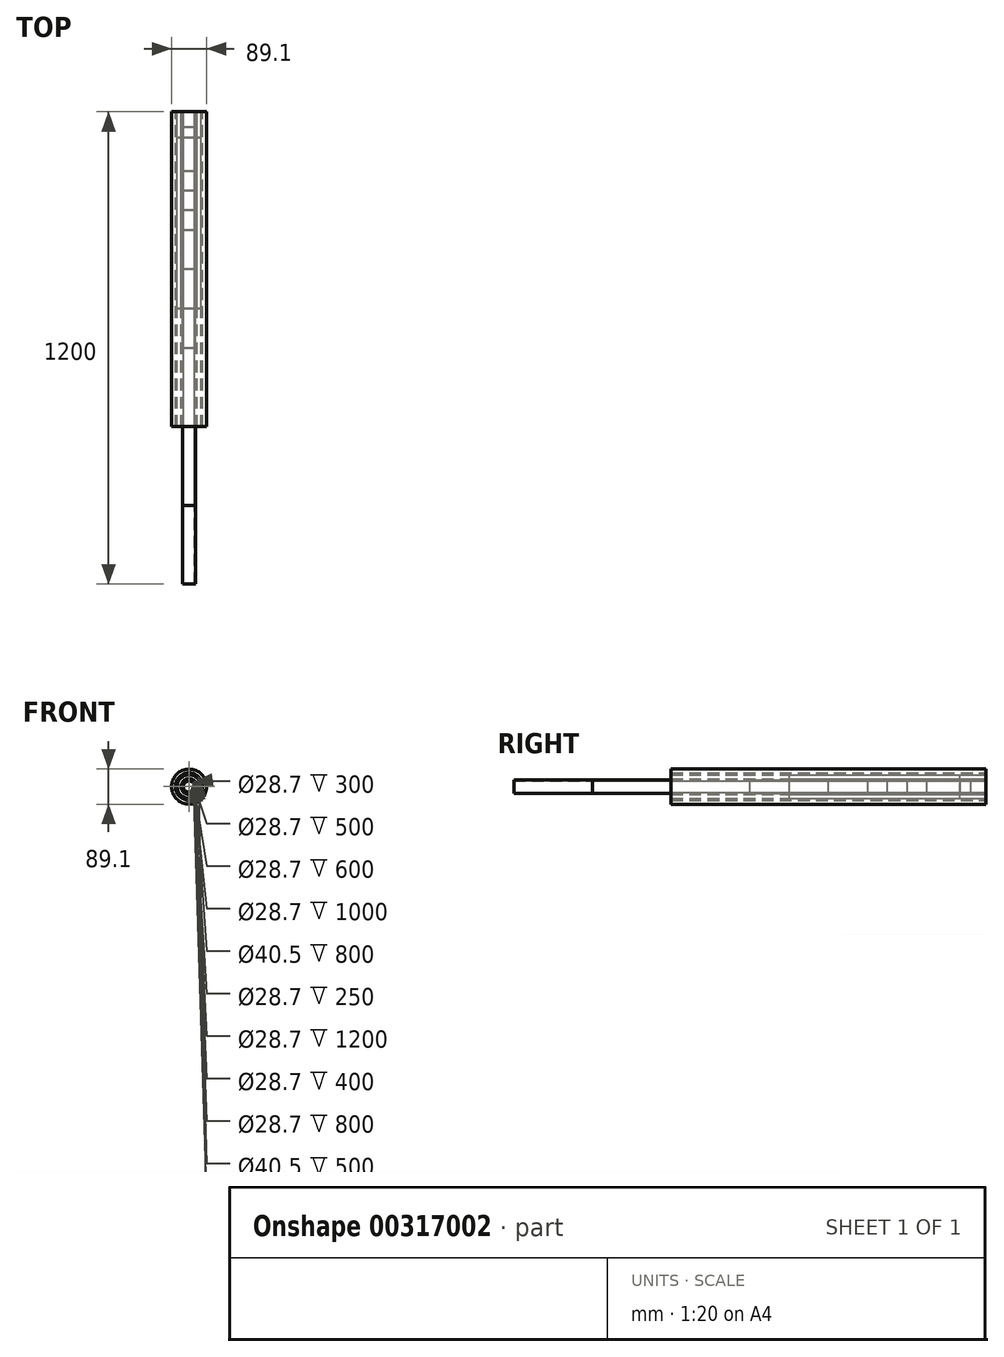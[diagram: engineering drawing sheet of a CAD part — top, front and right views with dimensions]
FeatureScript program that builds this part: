
annotation { "Feature Type Name" : "Feature", "Feature Type Description" : "" }
export const myFeature = defineFeature(function(context is Context, id is Id, definition is map)
    precondition{}
    {
        {
            var Q0;
            Q0=qCreatedBy(makeId("Front.planeOp"),FACE);
            var sketch = newSketch(context, id + "F0", { "sketchPlane" : qUnion([Q0])});
            skCircle(sketch, "E0", {"center": v(0, 0) * mm, "radius": 17 * mm});
            skCircle(sketch, "E1", {"center": v(0, 0) * mm, "radius": 14.35 * mm});
            skSolve(sketch);
        }
        {
            var Q0;
            Q0=makeQuery(id+"F0.imprint","IMPRINT",FACE,{"disambiguationData":[TD([[makeQuery(id+"F0.imprint","IMPRINT",EDGE,{"derivedFrom":sQuery(id+"F0.wireOp",EDGE,"E0")}),1.0]])]});
            extrude(context, id + "F1", {"entities" : qUnion([Q0]), "depth" : 1000 * mm});
        }
        {
            var Q0;
            Q0=makeQuery(id+"F0.imprint","IMPRINT",FACE,{"disambiguationData":[TD([[makeQuery(id+"F0.imprint","IMPRINT",EDGE,{"derivedFrom":sQuery(id+"F0.wireOp",EDGE,"E0")}),1.0]])]});
            extrude(context, id + "F2", {"entities" : qUnion([Q0]), "depth" : 39 * mm});
        }
        {
            var Q0;
            Q0=makeQuery(id+"F0.imprint","IMPRINT",FACE,{"disambiguationData":[TD([[makeQuery(id+"F0.imprint","IMPRINT",EDGE,{"derivedFrom":sQuery(id+"F0.wireOp",EDGE,"E0")}),1.0]])]});
            extrude(context, id + "F3", {"entities" : qUnion([Q0]), "depth" : 600 * mm});
        }
        {
            var Q0;
            Q0=makeQuery(id+"F0.imprint","IMPRINT",FACE,{"disambiguationData":[TD([[makeQuery(id+"F0.imprint","IMPRINT",EDGE,{"derivedFrom":sQuery(id+"F0.wireOp",EDGE,"E0")}),1.0]])]});
            extrude(context, id + "F4", {"entities" : qUnion([Q0]), "depth" : 300 * mm});
        }
        {
            var Q0;
            Q0=makeQuery(id+"F0.imprint","IMPRINT",FACE,{"disambiguationData":[TD([[makeQuery(id+"F0.imprint","IMPRINT",EDGE,{"derivedFrom":sQuery(id+"F0.wireOp",EDGE,"E0")}),1.0]])]});
            extrude(context, id + "F5", {"entities" : qUnion([Q0]), "depth" : 500 * mm});
        }
        {
            var Q0;
            Q0 = qSketchRegion(id + "F0", true);
            extrude(context, id + "F6", {"entities" : qUnion([Q0]), "depth" : 65 * mm});
        }
        {
            var Q0;
            Q0=qCreatedBy(makeId("Front.planeOp"),FACE);
            var sketch = newSketch(context, id + "F7", { "sketchPlane" : qUnion([Q0])});
            skCircle(sketch, "E2", {"center": v(0, 0) * mm, "radius": 30.25 * mm});
            skCircle(sketch, "E3", {"center": v(0, 0) * mm, "radius": 20.25 * mm});
            skSolve(sketch);
        }
        {
            var Q0;
            Q0=qCreatedBy(makeId("Front.planeOp"),FACE);
            var sketch = newSketch(context, id + "F8", { "sketchPlane" : qUnion([Q0])});
            skCircle(sketch, "E4", {"center": v(0, 0) * mm, "radius": 44.55 * mm});
            skCircle(sketch, "E5", {"center": v(0, 0) * mm, "radius": 34.55 * mm});
            skSolve(sketch);
        }
        {
            var Q0;
            Q0=makeQuery(id+"F8.imprint","IMPRINT",FACE,{"disambiguationData":[TD([[makeQuery(id+"F8.imprint","IMPRINT",EDGE,{"derivedFrom":sQuery(id+"F8.wireOp",EDGE,"E4")}),1.0]])]});
            extrude(context, id + "F9", {"entities" : qUnion([Q0]), "depth" : 800 * mm});
        }
        {
            var Q0;
            Q0=makeQuery(id+"F7.imprint","IMPRINT",FACE,{"disambiguationData":[TD([[makeQuery(id+"F7.imprint","IMPRINT",EDGE,{"derivedFrom":sQuery(id+"F7.wireOp",EDGE,"E2")}),1.0]])]});
            extrude(context, id + "F10", {"entities" : qUnion([Q0]), "depth" : 66 * mm});
        }
        {
            var Q0;
            Q0=makeQuery(id+"F0.imprint","IMPRINT",FACE,{"disambiguationData":[TD([[makeQuery(id+"F0.imprint","IMPRINT",EDGE,{"derivedFrom":sQuery(id+"F0.wireOp",EDGE,"E0")}),1.0]])]});
            extrude(context, id + "F11", {"entities" : qUnion([Q0]), "depth" : 200 * mm});
        }
        {
            var Q0;
            Q0=makeQuery(id+"F0.imprint","IMPRINT",FACE,{"disambiguationData":[TD([[makeQuery(id+"F0.imprint","IMPRINT",EDGE,{"derivedFrom":sQuery(id+"F0.wireOp",EDGE,"E0")}),1.0]])]});
            var Q1;
            Q1=sQuery(id+"F0.wireOp",EDGE,"E0");
            var Q2;
            Q2=sQuery(id+"F0.wireOp",EDGE,"E1");
            extrude(context, id + "F12", {"entities" : qUnion([Q0]), "surfaceEntities" : qUnion([Q1, Q2]), "depth" : 150 * mm});
        }
        {
            var Q0;
            Q0=makeQuery(id+"F7.imprint","IMPRINT",FACE,{"disambiguationData":[TD([[makeQuery(id+"F7.imprint","IMPRINT",EDGE,{"derivedFrom":sQuery(id+"F7.wireOp",EDGE,"E2")}),1.0]])]});
            extrude(context, id + "F13", {"entities" : qUnion([Q0]), "depth" : 500 * mm});
        }
        {
            var Q0;
            Q0=makeQuery(id+"F0.imprint","IMPRINT",FACE,{"disambiguationData":[TD([[makeQuery(id+"F0.imprint","IMPRINT",EDGE,{"derivedFrom":sQuery(id+"F0.wireOp",EDGE,"E0")}),1.0]])]});
            extrude(context, id + "F14", {"entities" : qUnion([Q0]), "depth" : 400 * mm});
        }
        {
            var Q0;
            Q0=makeQuery(id+"F0.imprint","IMPRINT",FACE,{"disambiguationData":[TD([[makeQuery(id+"F0.imprint","IMPRINT",EDGE,{"derivedFrom":sQuery(id+"F0.wireOp",EDGE,"E0")}),1.0]])]});
            extrude(context, id + "F15", {"entities" : qUnion([Q0]), "depth" : 800 * mm});
        }
        {
            var Q0;
            Q0=makeQuery(id+"F0.imprint","IMPRINT",FACE,{"disambiguationData":[TD([[makeQuery(id+"F0.imprint","IMPRINT",EDGE,{"derivedFrom":sQuery(id+"F0.wireOp",EDGE,"E0")}),1.0]])]});
            extrude(context, id + "F16", {"entities" : qUnion([Q0]), "depth" : 250 * mm});
        }
        {
            var Q0;
            Q0=makeQuery(id+"F0.imprint","IMPRINT",FACE,{"disambiguationData":[TD([[makeQuery(id+"F0.imprint","IMPRINT",EDGE,{"derivedFrom":sQuery(id+"F0.wireOp",EDGE,"E0")}),1.0]])]});
            extrude(context, id + "F17", {"entities" : qUnion([Q0]), "depth" : 1200 * mm});
        }
        {
            var Q0;
            Q0=makeQuery(id+"F7.imprint","IMPRINT",FACE,{"disambiguationData":[TD([[makeQuery(id+"F7.imprint","IMPRINT",EDGE,{"derivedFrom":sQuery(id+"F7.wireOp",EDGE,"E2")}),1.0]])]});
            extrude(context, id + "F18", {"entities" : qUnion([Q0]), "depth" : 800 * mm});
        }
    });
